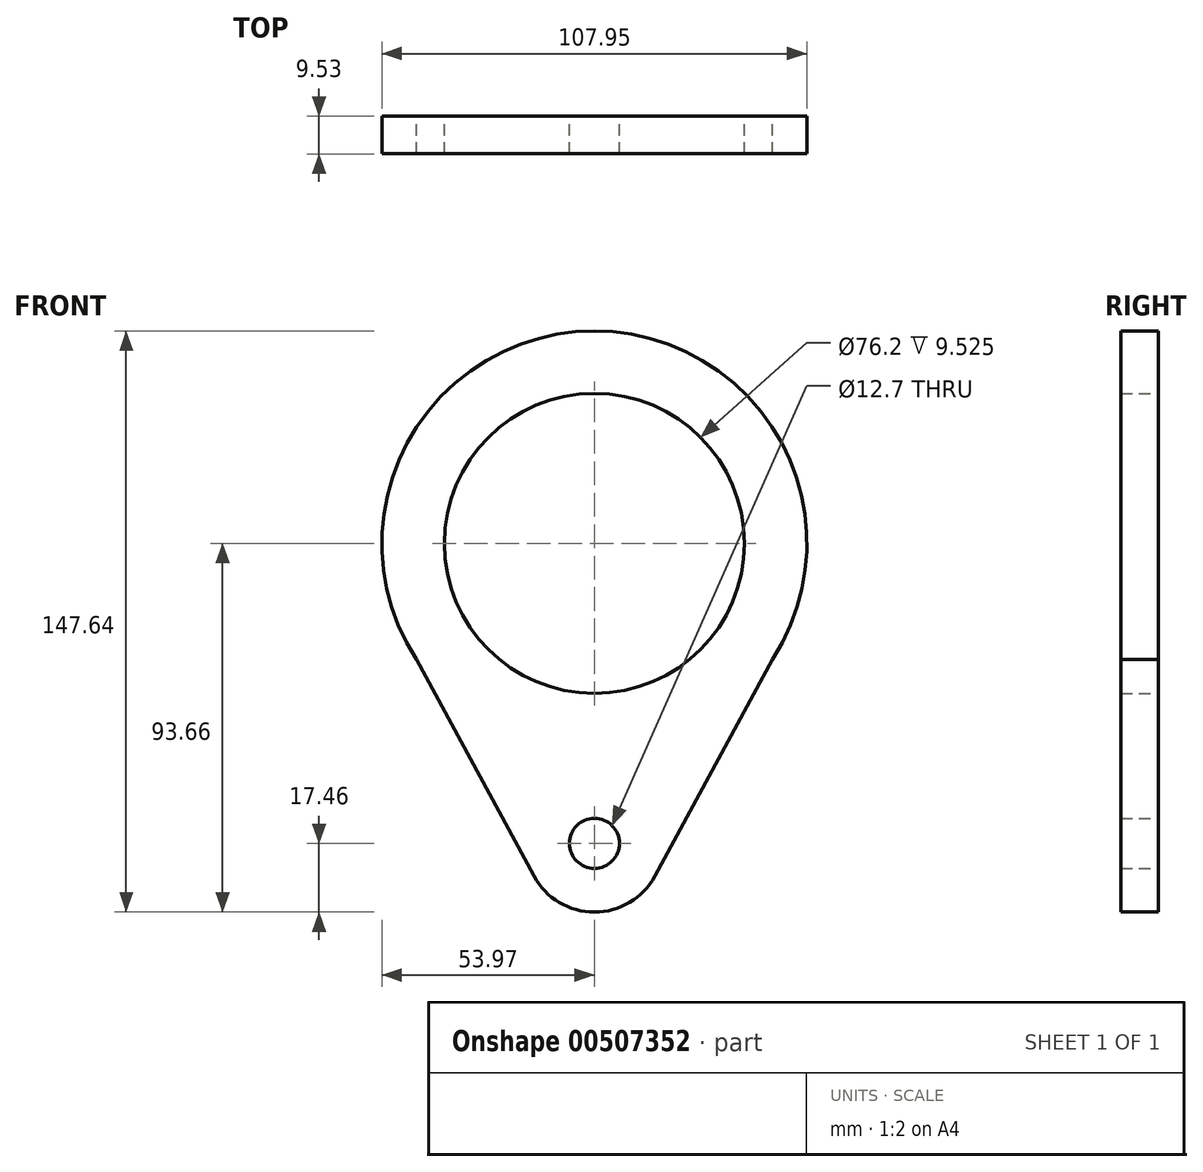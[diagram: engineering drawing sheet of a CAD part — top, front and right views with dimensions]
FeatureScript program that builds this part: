
annotation { "Feature Type Name" : "Feature", "Feature Type Description" : "" }
export const myFeature = defineFeature(function(context is Context, id is Id, definition is map)
    precondition{}
    {
        {
            var Q0;
            Q0=qCreatedBy(makeId("Front.planeOp"),FACE);
            var sketch = newSketch(context, id + "F0", { "sketchPlane" : qUnion([Q0])});
            skCircle(sketch, "E0", {"center": v(0, 0) * mm, "radius": 53.98 * mm});
            skCircle(sketch, "E1", {"center": v(0, -76.2) * mm, "radius": 6.35 * mm});
            skCircle(sketch, "E2", {"center": v(0, -76.2) * mm, "radius": 17.46 * mm});
            skCircle(sketch, "E3", {"center": v(0, 0) * mm, "radius": 38.1 * mm});
            skLineSegment(sketch, "E4", {"start": v(-45.22, -29.47) * mm, "end": v(-15.35, -84.53) * mm});
            skLineSegment(sketch, "E5.MirrorCS", {"start": v(45.22, -29.47) * mm, "end": v(15.35, -84.53) * mm});
            skSolve(sketch);
        }
        {
            var Q0;
            Q0=makeQuery(id+"F0.imprint","IMPRINT",FACE,{"disambiguationData":[TD([[makeQuery(id+"F0.imprint","IMPRINT",EDGE,{"derivedFrom":sQuery(id+"F0.wireOp",EDGE,"E3")}),-1.0]])]});
            var Q1;
            {var subQ0=sQuery(id+"F0.wireOp",EDGE,"E4");Q1=makeQuery(id+"F0.imprint","IMPRINT",FACE,{"disambiguationData":[TD([[makeQuery(id+"F0.imprint","IMPRINT",EDGE,{"derivedFrom":subQ0}),1.0]])]});}
            var Q2;
            Q2=makeQuery(id+"F0.imprint","IMPRINT",FACE,{"disambiguationData":[TD([[makeQuery(id+"F0.imprint","IMPRINT",EDGE,{"derivedFrom":sQuery(id+"F0.wireOp",EDGE,"E1")}),-1.0]])]});
            extrude(context, id + "F1", {"entities" : qUnion([Q0, Q1, Q2]), "depth" : 9.52 * mm});
        }
    });
